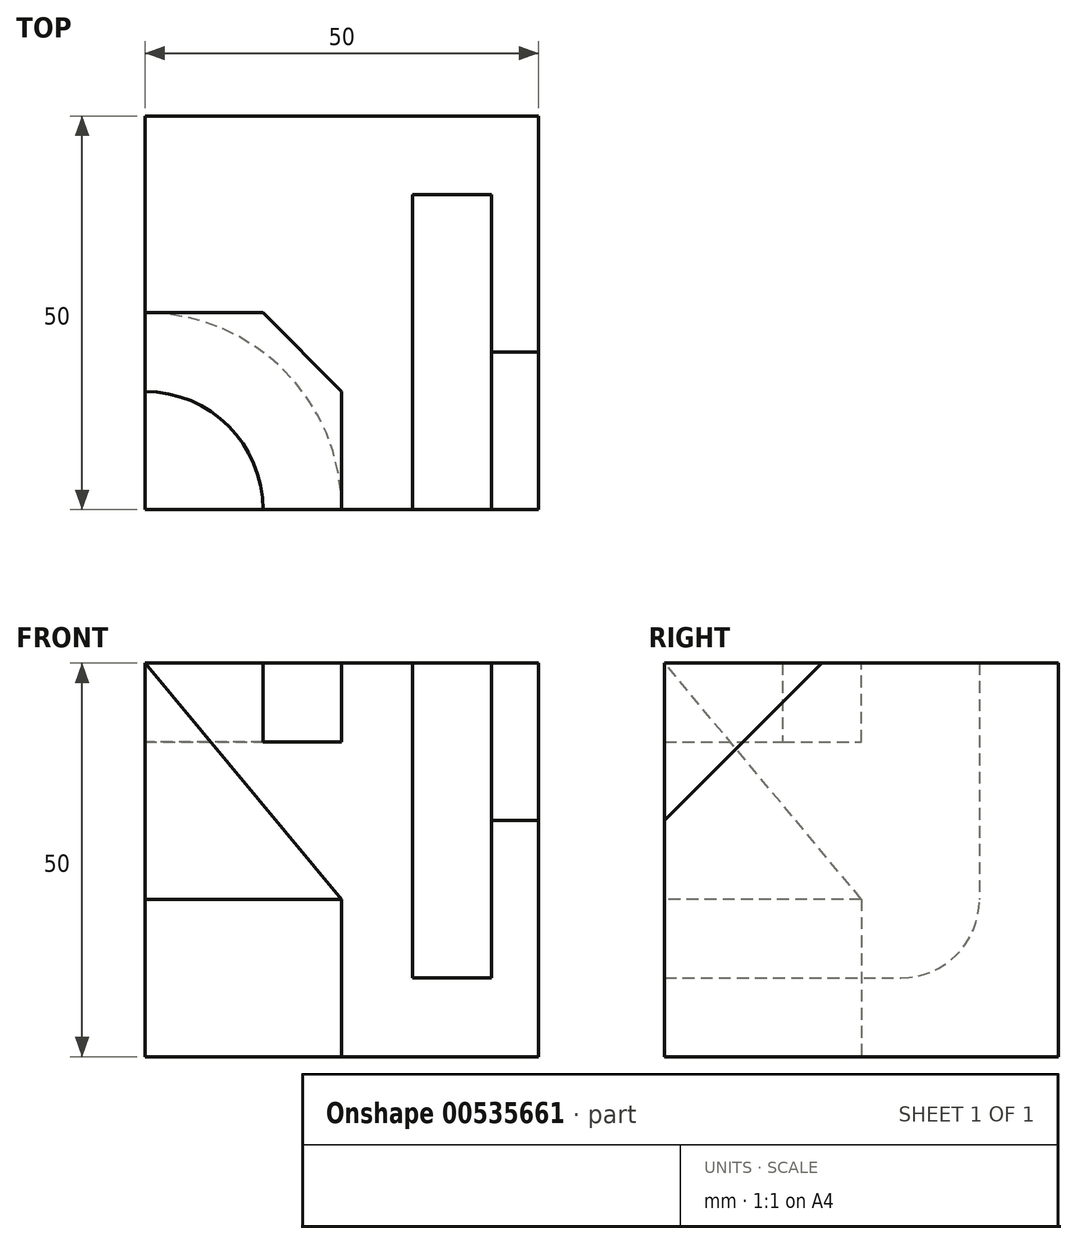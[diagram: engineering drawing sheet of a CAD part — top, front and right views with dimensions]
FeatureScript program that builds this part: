
annotation { "Feature Type Name" : "Feature", "Feature Type Description" : "" }
export const myFeature = defineFeature(function(context is Context, id is Id, definition is map)
    precondition{}
    {
        {
            var Q0;
            Q0=qCreatedBy(makeId("Top.planeOp"),FACE);
            var sketch = newSketch(context, id + "F0", { "sketchPlane" : qUnion([Q0])});
            skLineSegment(sketch, "E0.bottom", {"start": v(0, 0) * mm, "end": v(50, 0) * mm});
            skLineSegment(sketch, "E0.top", {"start": v(0, 50) * mm, "end": v(50, 50) * mm});
            skLineSegment(sketch, "E0.left", {"start": v(0, 0) * mm, "end": v(0, 50) * mm});
            skLineSegment(sketch, "E0.right", {"start": v(50, 0) * mm, "end": v(50, 50) * mm});
            skSolve(sketch);
        }
        {
            var Q0;
            Q0 = qSketchRegion(id + "F0", true);
            extrude(context, id + "F1", {"entities" : qUnion([Q0]), "depth" : 50 * mm, "offsetDistance" : 25 * mm});
        }
        {
            var Q0;
            Q0=makeQuery(id+"F1.opExtrude","CAP_FACE",FACE,{"disambiguationData":[OSD([sQuery(id+"F0.wireOp",EDGE,"E0.bottom"),sQuery(id+"F0.wireOp",EDGE,"E0.top"),sQuery(id+"F0.wireOp",EDGE,"E0.left"),sQuery(id+"F0.wireOp",EDGE,"E0.right")])],"isStart":true});
            var sketch = newSketch(context, id + "F2", { "sketchPlane" : qUnion([Q0])});
            skCircle(sketch, "E1", {"center": v(0, 0) * mm, "radius": 25 * mm});
            skSolve(sketch);
        }
        {
            var Q0;
            Q0 = qSketchRegion(id + "F2", true);
            extrude(context, id + "F3", {"entities" : qUnion([Q0]), "operationType" : NewBodyOperationType.REMOVE, "oppositeDirection" : true, "depth" : 20 * mm, "offsetDistance" : 25 * mm});
        }
        {
            var Q0;
            Q0=qCreatedBy(makeId("Right.planeOp"),FACE);
            cPlane(context, id + "F4", {"entities" : qUnion([Q0]), "cplaneType" : CPlaneType.OFFSET, "offset" : 34 * mm, "width" : 150 * mm, "height" : 150 * mm});
        }
        {
            var Q0;
            Q0=qCreatedBy(id+"F4.planeOp",FACE);
            var sketch = newSketch(context, id + "F5", { "sketchPlane" : qUnion([Q0])});
            skLineSegment(sketch, "E2.bottom", {"start": v(0, 50) * mm, "end": v(40, 50) * mm});
            skLineSegment(sketch, "E2.top", {"start": v(0, 10) * mm, "end": v(40, 10) * mm});
            skLineSegment(sketch, "E2.left", {"start": v(0, 50) * mm, "end": v(0, 10) * mm});
            skLineSegment(sketch, "E2.right", {"start": v(40, 50) * mm, "end": v(40, 10) * mm});
            skSolve(sketch);
        }
        {
            var Q0;
            Q0 = qSketchRegion(id + "F5", true);
            extrude(context, id + "F6", {"entities" : qUnion([Q0]), "operationType" : NewBodyOperationType.REMOVE, "depth" : 10 * mm, "offsetDistance" : 25 * mm});
        }
        {
            var Q0;
            Q0=makeQuery(id+"F6.boolean.opBoolean","COPY",EDGE,{"derivedFrom":makeQuery(id+"F6.opExtrude","SWEPT_EDGE",EDGE,{"disambiguationData":[OSD([sQuery(id+"F5.wireOp",EDGE,"E2.top"),sQuery(id+"F5.wireOp",EDGE,"E2.right")])]})});
            fillet(context, id + "F7", {"entities" : qUnion([Q0]), "radius" : 10 * mm, "tangentPropagation" : true, "allowEdgeOverflow" : false});
        }
        {
            var Q0;
            Q0=makeQuery(id+"F1.opExtrude","SWEPT_FACE",FACE,{"disambiguationData":[OSD([sQuery(id+"F0.wireOp",EDGE,"E0.right")])]});
            var sketch = newSketch(context, id + "F8", { "sketchPlane" : qUnion([Q0])});
            skLineSegment(sketch, "E3", {"start": v(0, 50) * mm, "end": v(20, 50) * mm});
            skLineSegment(sketch, "E4", {"start": v(20, 50) * mm, "end": v(0, 30) * mm});
            skLineSegment(sketch, "E5", {"start": v(0, 30) * mm, "end": v(0, 50) * mm});
            skSolve(sketch);
        }
        {
            var Q0;
            Q0 = qSketchRegion(id + "F8", true);
            extrude(context, id + "F9", {"entities" : qUnion([Q0]), "operationType" : NewBodyOperationType.REMOVE, "oppositeDirection" : true, "depth" : 6 * mm, "offsetDistance" : 25 * mm});
        }
        {
            var Q0;
            Q0=makeQuery(id+"F1.opExtrude","CAP_FACE",FACE,{"disambiguationData":[OSD([sQuery(id+"F0.wireOp",EDGE,"E0.bottom"),sQuery(id+"F0.wireOp",EDGE,"E0.top"),sQuery(id+"F0.wireOp",EDGE,"E0.left"),sQuery(id+"F0.wireOp",EDGE,"E0.right")])],"isStart":false});
            var sketch = newSketch(context, id + "F10", { "sketchPlane" : qUnion([Q0])});
            skLineSegment(sketch, "E6.bottom", {"start": v(0, 0) * mm, "end": v(25, 0) * mm});
            skLineSegment(sketch, "E6.top", {"start": v(0, 25) * mm, "end": v(25, 25) * mm});
            skLineSegment(sketch, "E6.left", {"start": v(0, 0) * mm, "end": v(0, 25) * mm});
            skLineSegment(sketch, "E6.right", {"start": v(25, 0) * mm, "end": v(25, 25) * mm});
            skSolve(sketch);
        }
        {
            var Q0;
            Q0 = qSketchRegion(id + "F10", true);
            extrude(context, id + "F11", {"entities" : qUnion([Q0]), "operationType" : NewBodyOperationType.REMOVE, "oppositeDirection" : true, "depth" : 10 * mm, "offsetDistance" : 25 * mm});
        }
        {
            var Q0;
            Q0=makeQuery(id+"F11.boolean.opBoolean","COPY",EDGE,{"derivedFrom":makeQuery(id+"F11.opExtrude","SWEPT_EDGE",EDGE,{"disambiguationData":[OSD([sQuery(id+"F10.wireOp",EDGE,"E6.top"),sQuery(id+"F10.wireOp",EDGE,"E6.right")])]})});
            chamfer(context, id + "F12", {"entities" : qUnion([Q0]), "width" : 10 * mm, "tangentPropagation" : true});
        }
        {
            var Q0;
            Q0=makeQuery(id+"F11.boolean.opBoolean","COPY",FACE,{"derivedFrom":makeQuery(id+"F11.opExtrude","CAP_FACE",FACE,{"disambiguationData":[OSD([sQuery(id+"F10.wireOp",EDGE,"E6.bottom"),sQuery(id+"F10.wireOp",EDGE,"E6.top"),sQuery(id+"F10.wireOp",EDGE,"E6.left"),sQuery(id+"F10.wireOp",EDGE,"E6.right")])],"isStart":false})});
            var sketch = newSketch(context, id + "F13", { "sketchPlane" : qUnion([Q0])});
            skPoint(sketch, "E7", {"position": v(0, 15) * mm});
            skPoint(sketch, "E8", {"position": v(15, 0) * mm});
            skArc(sketch, "E9", {"start": v(15, 0) * mm, "mid": v(10.6, 10.6) * mm, "end": v(0, 15) * mm});
            skLineSegment(sketch, "E10", {"start": v(15, 0) * mm, "end": v(0, 0) * mm});
            skSolve(sketch);
        }
        {
            var Q0;
            Q0 = qSketchRegion(id + "F13", true);
            var Q1;
            {var subQ0=sQuery(id+"F13.wireOp",EDGE,"E9");Q1=makeQuery(id+"F13.imprint","IMPRINT",FACE,{"disambiguationData":[TD([[makeQuery(id+"F13.imprint","IMPRINT",EDGE,{"derivedFrom":subQ0}),1.0]])]});}
            extrude(context, id + "F14", {"entities" : qUnion([Q0, Q1]), "operationType" : NewBodyOperationType.ADD, "depth" : 10 * mm, "offsetDistance" : 25 * mm});
        }
        {
            var Q0;
            Q0=makeQuery(id+"F14.boolean.opBoolean","MERGE",FACE,{"derivedFrom":[makeQuery(id+"F1.opExtrude","SWEPT_FACE",FACE,{"disambiguationData":[OSD([sQuery(id+"F0.wireOp",EDGE,"E0.bottom")])]}),makeQuery(id+"F14.opExtrude","SWEPT_FACE",FACE,{"disambiguationData":[OSD([sQuery(id+"F13.wireOp",EDGE,"E10")])]})]});
            var sketch = newSketch(context, id + "F15", { "sketchPlane" : qUnion([Q0])});
            skLineSegment(sketch, "E11", {"start": v(0, 50) * mm, "end": v(25, 20) * mm});
            skLineSegment(sketch, "E12", {"start": v(25, 20) * mm, "end": v(0, 20) * mm});
            skLineSegment(sketch, "E13", {"start": v(0, 20) * mm, "end": v(0, 50) * mm});
            skSolve(sketch);
        }
        {
            var Q1;
            Q1=makeQuery(id+"F3.boolean.opBoolean","COPY",FACE,{"derivedFrom":makeQuery(id+"F3.opExtrude","CAP_FACE",FACE,{"disambiguationData":[OSD([sQuery(id+"F2.wireOp",EDGE,"E1")])],"isStart":false})});
            var Q2;
            Q2=sQuery(id+"F15.wireOp",VERTEX,"E11.start");
            loft(context, id + "F16", {"operationType" : NewBodyOperationType.REMOVE, "sheetProfilesArray" : [{ "sheetProfileEntities" : qUnion([Q1]) }, { "sheetProfileEntities" : qUnion([Q2]) }]});
        }
    });
